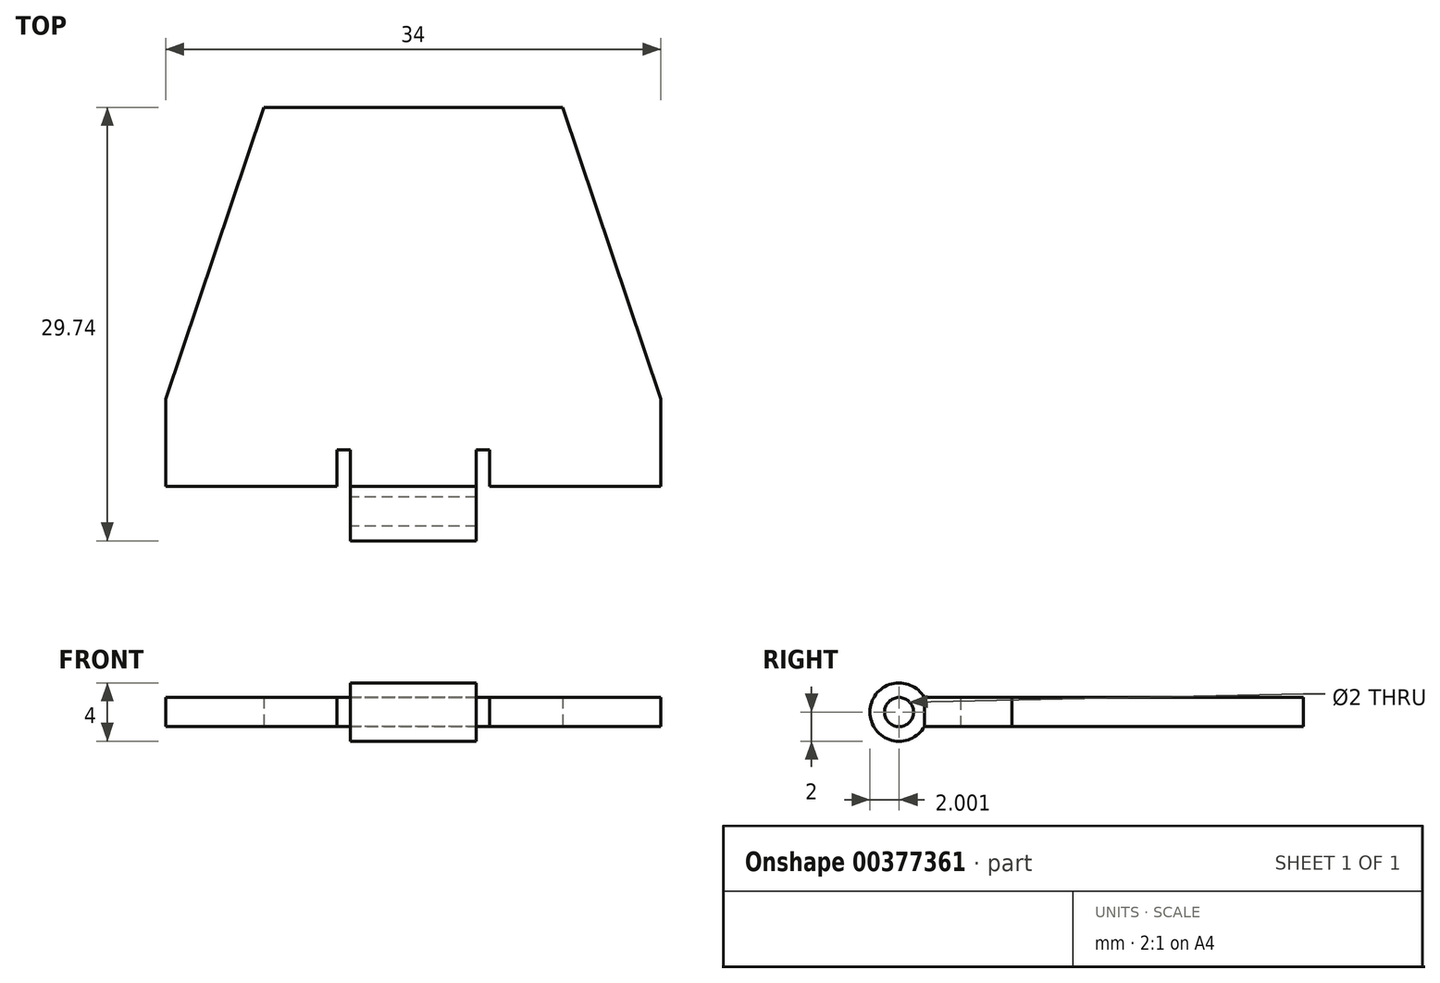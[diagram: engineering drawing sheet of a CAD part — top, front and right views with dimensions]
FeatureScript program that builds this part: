
annotation { "Feature Type Name" : "Feature", "Feature Type Description" : "" }
export const myFeature = defineFeature(function(context is Context, id is Id, definition is map)
    precondition{}
    {
        {
            var Q0;
            Q0=qCreatedBy(makeId("Top.planeOp"),FACE);
            var sketch = newSketch(context, id + "F0", { "sketchPlane" : qUnion([Q0])});
            skLineSegment(sketch, "E0", {"start": v(17, 18.96) * mm, "end": v(17, 24.96) * mm});
            skLineSegment(sketch, "E1", {"start": v(17, 24.96) * mm, "end": v(10.25, 44.96) * mm});
            skLineSegment(sketch, "E2", {"start": v(10.25, 44.96) * mm, "end": v(0, 44.96) * mm});
            skLineSegment(sketch, "E3", {"start": v(0, 44.96) * mm, "end": v(0, -32.85) * mm, "construction": true});
            skLineSegment(sketch, "E4.MirrorCS", {"start": v(-10.25, 44.96) * mm, "end": v(0, 44.96) * mm});
            skLineSegment(sketch, "E5.MirrorCS", {"start": v(-17, 24.96) * mm, "end": v(-10.25, 44.96) * mm});
            skLineSegment(sketch, "E6.MirrorCS", {"start": v(-17, 18.96) * mm, "end": v(-17, 24.96) * mm});
            skLineSegment(sketch, "E7.MirrorCS", {"start": v(8.03, 18.96) * mm, "end": v(8.03, 44.96) * mm, "construction": true});
            skLineSegment(sketch, "E8", {"start": v(0, 18.96) * mm, "end": v(-17, 18.96) * mm});
            skLineSegment(sketch, "E9.MirrorCS", {"start": v(0, 18.96) * mm, "end": v(17, 18.96) * mm});
            skSolve(sketch);
        }
        {
            var Q0;
            Q0=qSketchRegion(id+"F0",true);
            extrude(context, id + "F1", {"entities" : qUnion([Q0]), "depth" : 2 * mm});
        }
        {
            var Q0;
            Q0=qCreatedBy(makeId("Right.planeOp"),FACE);
            var sketch = newSketch(context, id + "F2", { "sketchPlane" : qUnion([Q0])});
            skCircle(sketch, "E10", {"center": v(17.22, 1) * mm, "radius": 1 * mm});
            skPoint(sketch, "E10.centerSnap0", {"position": v(1.16, 1) * mm});
            skCircle(sketch, "E11.0", {"center": v(17.22, 1) * mm, "radius": 2 * mm});
            skSolve(sketch);
        }
        {
            var Q0;
            Q0=qSketchRegion(id+"F2",true);
            extrude(context, id + "F3", {"entities" : qUnion([Q0]), "operationType" : NewBodyOperationType.ADD, "depth" : (8.65 / 2) * mm, "hasSecondDirection" : true, "secondDirectionOppositeDirection" : true, "secondDirectionDepth" : (8.65 / 2) * mm});
        }
        {
            var Q0;
            Q0=makeQuery(id+"F4kdEE4rauptjU6_2.boolean.opBoolean","MERGE",FACE,{"derivedFrom":[makeQuery(id+"F1.opExtrude","CAP_FACE",FACE,{"disambiguationData":[OSD([sQuery(id+"F0.wireOp",EDGE,"E0"),sQuery(id+"F0.wireOp",EDGE,"E1"),sQuery(id+"F0.wireOp",EDGE,"E2"),sQuery(id+"F0.wireOp",EDGE,"E4.MirrorCS"),sQuery(id+"F0.wireOp",EDGE,"E5.MirrorCS"),sQuery(id+"F0.wireOp",EDGE,"E6.MirrorCS"),sQuery(id+"F0.wireOp",EDGE,"E8"),sQuery(id+"F0.wireOp",EDGE,"E9.MirrorCS")])],"isStart":false}),makeQuery(id+"F4kdEE4rauptjU6_2.opExtrude","SWEPT_FACE",FACE,{"disambiguationData":[OSD([sQuery(id+"FaDdaZCdBGJOY1z_2.wireOp",EDGE,"JDN6bjty-8Cl0-Nnsx-bK5f-Bjns8TjWKGfM.bottom")])]})]});
            var sketch = newSketch(context, id + "F4", { "sketchPlane" : qUnion([Q0])});
            skLineSegment(sketch, "E12.bottom", {"start": v(-4.33, 18.96) * mm, "end": v(-5.22, 18.96) * mm});
            skLineSegment(sketch, "E12.top", {"start": v(-4.33, 21.46) * mm, "end": v(-5.22, 21.46) * mm});
            skLineSegment(sketch, "E12.left", {"start": v(-4.33, 18.96) * mm, "end": v(-4.33, 21.46) * mm});
            skLineSegment(sketch, "E12.right", {"start": v(-5.22, 18.96) * mm, "end": v(-5.22, 21.46) * mm});
            skLineSegment(sketch, "E13.MirrorCS", {"start": v(5.22, 18.96) * mm, "end": v(5.22, 21.46) * mm});
            skLineSegment(sketch, "E14.MirrorCS", {"start": v(4.33, 18.96) * mm, "end": v(4.33, 21.46) * mm});
            skLineSegment(sketch, "E15.MirrorCS", {"start": v(4.33, 21.46) * mm, "end": v(5.22, 21.46) * mm});
            skLineSegment(sketch, "E16.MirrorCS", {"start": v(4.33, 18.96) * mm, "end": v(5.22, 18.96) * mm});
            skSolve(sketch);
        }
        {
            var Q0;
            Q0 = qSketchRegion(id + "F4", true);
            extrude(context, id + "F5", {"entities" : qUnion([Q0]), "operationType" : NewBodyOperationType.REMOVE, "endBound" : BoundingType.THROUGH_ALL, "oppositeDirection" : true, "depth" : 25 * mm});
        }
    });
